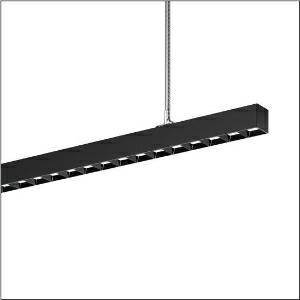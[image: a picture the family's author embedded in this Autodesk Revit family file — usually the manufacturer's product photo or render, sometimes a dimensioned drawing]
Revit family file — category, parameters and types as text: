
# Revit family: silica_r__21_51mx34dc3dbb_b9b0
name_source: partatom
category: Lighting Fixtures
units: mm (PartAtom-declared; Revit-internal decimal feet)

## family parameters
Cut with Voids When Loaded = No
Host = Face
Light Source = No
Part Type = Normal
Room Calculation Point = No
Round Connector Dimension = Use Diameter
Shared = No

## types (1)
- --- (1 x LED, 19200 lm, 129.1 W, 3000K)
    Apparent Load = 129 VA
    CIE Flux Codes = 74 94 99 56 100
    Color Rendering = 80
    Color Temperature = 3000K
    Default Elevation = 1800 mm
    Description = Silica® 21, office luminaire, primary light control with darklight reflector, of PMMA, black, light emission: direct/indirect distribution, primary light characteristic: asymmetric, installation type: suspended mounting, LED, rated luminous flux: 19.200lm, luminous efficacy: 149lm/W, light colour: 830, colour temperature: 3000K, control gear: DALI 2, with terminal, 3+2-pole, max. 2.5mm², mains connection: 220..240V, AC, 50/60Hz, rated input power: 129.1W, luminaire housing, of aluminium, matt jet black (RAL 9005), length: 3.004mm, width: 53mm, height: 53mm, protection rating (complete): IP20, insulation class (complete): insulation class I (protective earthing), certification: CE, permissible operating ambient temperature: 0..+35°C, standard: EN 50419, packaging unit: 1 piece
    Height = 53 mm
    Lamp = 1 x LED
    Lamp Light Flux = 19200 lm
    Lamp Power = 129.1 W
    Lamp count = 1
    Length = 3004 mm
    Luminous efficacy = 149 lm/W
    Manufacturer = Siteco
    ModVariant = No
    Model = 51MX34DC3DBB
    Mounting Place = Ceiling
    Mounting Type = Pendant
    Number of Poles = 1
    OnlyDefault = Yes
    Power Factor = 1
    Product Name = Silica® 21
    Product group = office luminaire | ceiling pendant
    ProductGroupID = 904
    Protection Class = Protection class I
    Protection Degree = IP 20
    RLX_Detail_Level = 1
    RLX_Emergency_Light_Flux = 0 lm
    RLX_Emergency_Type = 0
    RLX_Emergency_Type_DB = No
    RlxData = <blob elided: 67845 chars, md5=a17d7678>
    Socket = socket
    Standby Power = 0 W
    System Light Flux = 19200 lm
    System Power = 129 W
    Type Comments = factory setting: luminous flux: 100 % | dim-lin: 254 | 448 mA
    Type Image = l_1335852.jpg
    URL = http://relux.com
    VarID = @adj_120052
    Voltage = 0 V
    Weight = 0.00 kg
    Width = 53 mm

## geometry (parser evidence)
native form markers: Blend x4, Sweep x11
no freeform markers — native parametric forms only
